# Revit family: Geräteeinsätze GES_Geräteeinsatz_Revisionsabdeckung ZES9
name_source: partatom
category: Generic Models
revit_build: Autodesk Revit 2015 (Build: 20140606_1530(x64)
units: mm (PartAtom-declared; Revit-internal decimal feet)

## types (3) — shared parameters
Height = 65 mm  [stored 0.213255 ft]
Manufacturer = OBO Bettermann
URL = http://www.obo-bettermann.com
Width = 264 mm  [stored 0.866142 ft]
Width 2 = 242 mm  [stored 0.793963 ft]

## per-type parameters (varying)
| type | GTIN | Manufacturer Art. No. | Material |
| ZES9-2 U10T 9011 | 4012195870272 | 7406674 | Plastic RAL 9011 |
| ZES9-2 U10T 7011 | 4012195870265 | 7406672 | Plastic RAL 7011 |
| ZES9-2 U10T 1019 | 4012195870289 | 7406676 | Plastic RAL 1019 |

note: column(s) folded — value = type name in every type: Article Type

note: [stored X ft] marks values corroborated as IEEE doubles in the binary element streams (Revit-internal decimal feet)

## geometry (parser evidence)
native form markers: Sweep x2
no freeform markers — native parametric forms only
